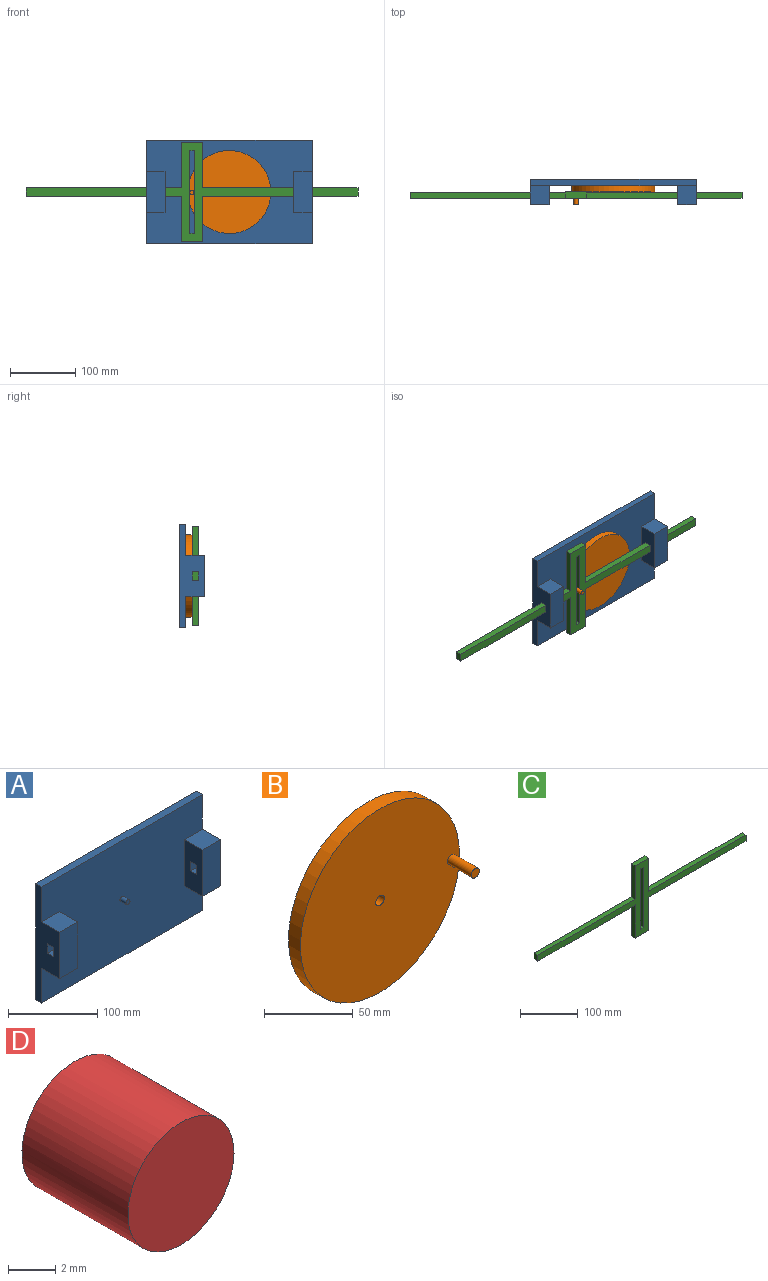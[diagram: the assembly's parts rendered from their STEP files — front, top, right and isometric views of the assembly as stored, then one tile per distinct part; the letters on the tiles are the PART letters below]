
ASSEMBLY  parts=4 mates=4
PART A: 24 faces, bbox 254x38.1x158.8 mm
  f0: cylinder r=3.17mm len=9.53mm, axis (0,1,0), area 190mm2, adj f6,f23
  f1: plane 158.75x38.1mm, normal (1,0,0), area 3205.6mm2, adj f2,f4,f5,f6,f7,f8,f10,f19
  f2: plane 254x9.53mm, normal (0,0,-1), area 2419.3mm2, adj f1,f3,f5,f6
  f3: plane 158.75x38.1mm, normal (-1,0,0), area 3205.6mm2, adj f2,f4,f5,f6,f11,f13,f14,f15
  f4: plane 254x9.53mm, normal (0,0,1), area 2419.3mm2, adj f1,f3,f5,f6
  f5: plane 254x158.75mm, normal (0,1,0), area 40322.5mm2, adj f1,f2,f3,f4
  f6: plane 254x158.75mm, normal (0,-1,0), area 36661.8mm2, adj f0,f1,f2,f3,f4,f7,f8,f9
  f7: plane 28.58x28.58mm, normal (0,0,-1), area 816.5mm2, adj f1,f6,f9,f10
  f8: plane 28.58x28.58mm, normal (0,0,1), area 816.5mm2, adj f1,f6,f9,f10
  f9: plane 63.5x28.58mm, normal (-1,0,0), area 1693.5mm2, adj f6,f7,f8,f10,f19,f20,f21,f22
  f10: plane 63.5x28.58mm, normal (0,-1,0), area 1814.5mm2, adj f1,f7,f8,f9
  f11: plane 28.58x28.58mm, normal (0,0,-1), area 816.5mm2, adj f3,f6,f12,f14
  f12: plane 63.5x28.58mm, normal (1,0,0), area 1693.5mm2, adj f6,f11,f13,f14,f15,f16,f17,f18
  f13: plane 28.58x28.58mm, normal (0,0,1), area 816.5mm2, adj f3,f6,f12,f14
  f14: plane 63.5x28.58mm, normal (0,-1,0), area 1814.5mm2, adj f3,f11,f12,f13
  f15: plane 28.58x12.7mm, normal (0,-1,0), area 362.9mm2, adj f3,f12,f17,f18
  f16: plane 28.58x12.7mm, normal (0,1,0), area 362.9mm2, adj f3,f12,f17,f18
  f17: plane 28.58x9.53mm, normal (0,0,1), area 272.2mm2, adj f3,f12,f15,f16
  f18: plane 28.58x9.53mm, normal (0,0,-1), area 272.2mm2, adj f3,f12,f15,f16
  f19: plane 28.58x12.7mm, normal (0,-1,0), area 362.9mm2, adj f1,f9,f21,f22
  f20: plane 28.58x12.7mm, normal (0,1,0), area 362.9mm2, adj f1,f9,f21,f22
  f21: plane 28.58x9.53mm, normal (0,0,1), area 272.2mm2, adj f1,f9,f19,f20
  f22: plane 28.58x9.53mm, normal (0,0,-1), area 272.2mm2, adj f1,f9,f19,f20
  f23: plane 6.35x6.35mm, normal (0,-1,0), area 31.7mm2, adj f0
PART B: 6 faces, bbox 127x28.6x127 mm
  f0: cylinder r=3.38mm len=9.53mm, axis (0,1,0), area 202.2mm2, adj f2,f3
  f1: cylinder r=63.5mm len=127mm, axis (0,1,0), area 3800.3mm2, adj f2,f3
  f2: plane 127x127mm, normal (0,-1,0), area 12600.2mm2, adj f0,f1,f4
  f3: plane 127x127mm, normal (0,1,0), area 12631.8mm2, adj f0,f1
  f4: cylinder r=3.17mm len=19.05mm, axis (0,1,0), area 380mm2, adj f2,f5
  f5: plane 6.35x6.35mm, normal (0,-1,0), area 31.7mm2, adj f4
PART C: 18 faces, bbox 508x9.5x152.4 mm
  f0: plane 9.53x7.16mm, normal (0,0,1), area 68.2mm2, adj f1,f15,f16,f17
  f1: plane 127x9.53mm, normal (1,0,0), area 1209.7mm2, adj f0,f2,f16,f17
  f2: plane 9.53x7.16mm, normal (0,0,-1), area 68.2mm2, adj f1,f15,f16,f17
  f3: plane 237.73x9.53mm, normal (0,0,1), area 2264.4mm2, adj f4,f14,f16,f17
  f4: plane 69.85x9.53mm, normal (1,0,0), area 665.3mm2, adj f3,f5,f16,f17
  f5: plane 32.54x9.53mm, normal (0,0,1), area 309.9mm2, adj f4,f6,f16,f17
  f6: plane 69.85x9.53mm, normal (-1,0,0), area 665.3mm2, adj f5,f7,f16,f17
  f7: plane 237.73x9.53mm, normal (0,0,1), area 2264.4mm2, adj f6,f8,f16,f17
  f8: plane 12.7x9.53mm, normal (-1,0,0), area 121mm2, adj f7,f9,f16,f17
  f9: plane 237.73x9.53mm, normal (0,0,-1), area 2264.4mm2, adj f8,f10,f16,f17
  f10: plane 69.85x9.53mm, normal (-1,0,0), area 665.3mm2, adj f9,f11,f16,f17
  f11: plane 32.54x9.53mm, normal (0,0,-1), area 309.9mm2, adj f10,f12,f16,f17
  f12: plane 69.85x9.53mm, normal (1,0,0), area 665.3mm2, adj f11,f13,f16,f17
  f13: plane 237.73x9.53mm, normal (0,0,-1), area 2264.4mm2, adj f12,f14,f16,f17
  f14: plane 12.7x9.53mm, normal (1,0,0), area 121mm2, adj f3,f13,f16,f17
  f15: plane 127x9.53mm, normal (-1,0,0), area 1209.7mm2, adj f0,f2,f16,f17
  f16: plane 508x152.4mm, normal (0,-1,0), area 10087.4mm2, adj f0,f1,f2,f3,f4,f5,f6,f7
  f17: plane 508x152.4mm, normal (0,1,0), area 10087.4mm2, adj f0,f1,f2,f3,f4,f5,f6,f7
PART D: 3 faces, bbox 6.4x6.4x6.4 mm
  f0: plane 6.35x6.35mm, normal (0,-1,0), area 31.7mm2, adj f1
  f1: cylinder r=3.17mm len=6.35mm, axis (0,1,0), area 126.7mm2, adj f0,f2
  f2: plane 6.35x6.35mm, normal (0,1,0), area 31.7mm2, adj f1
PLACE A at identity fixed
PLACE B rot(axis=(0,1,0),179deg) t=(0,0,0)mm
PLACE C t=(-114.29,0,0)mm
PLACE D rot(axis=(0,-1,0),90deg) t=(0,9.52,0)mm
MATE revolute B.f0 <-> D.f1  axis (0,-1,0) through (0,-9.52,0)mm
MATE revolute B.f0 <-> A.f0  axis (0,1,0) through (0,0,0)mm
MATE pin_slot B.f4 <-> C.f16  axis (0,1,0) through (-57.14,-19.05,-1.03)mm
MATE slider C.f8 <-> A.f12  axis (1,0,0) through (-311.14,-19.05,6.35)mm
